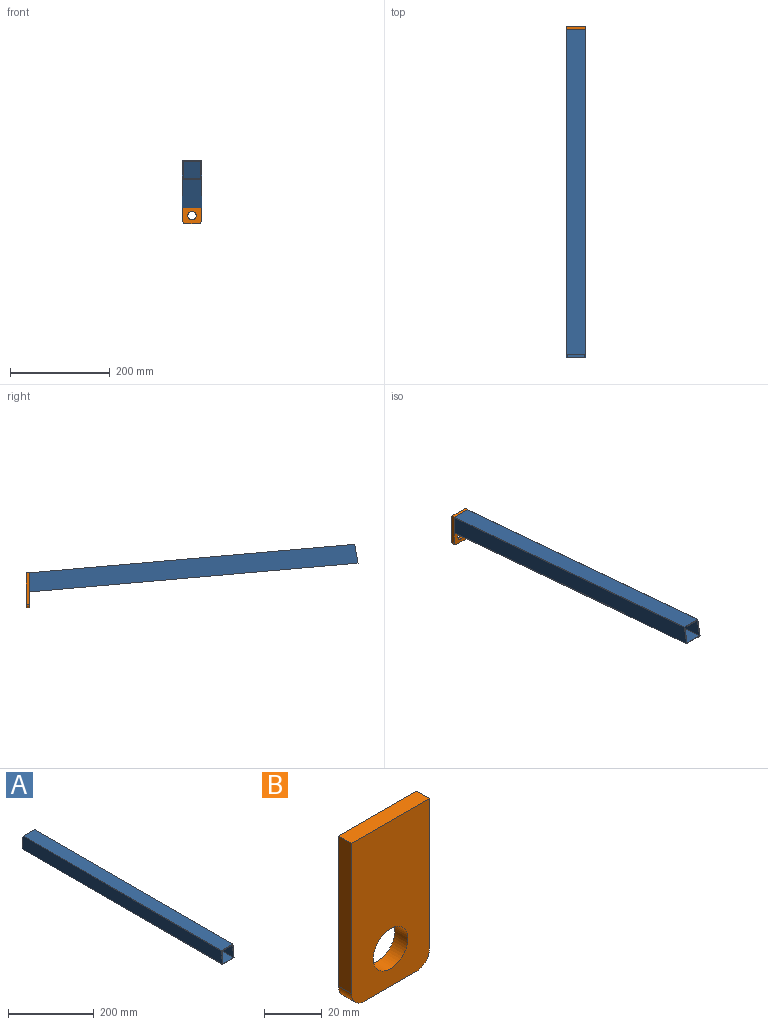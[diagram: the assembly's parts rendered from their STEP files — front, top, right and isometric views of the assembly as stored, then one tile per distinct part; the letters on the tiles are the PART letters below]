
ASSEMBLY  parts=2 mates=1
PART A: 10 faces, bbox 38.1x660.4x38.1 mm
  f0: plane 660.4x38.1mm, normal (1,0,0), area 25034.2mm2, adj f1,f7,f8,f9
  f1: plane 653.73x38.1mm, normal (0,0,1), area 24907.2mm2, adj f0,f5,f8,f9
  f2: plane 660.12x34.93mm, normal (1,0,0), area 22948.1mm2, adj f3,f6,f8,f9
  f3: plane 654.01x34.93mm, normal (0,0,-1), area 22841.3mm2, adj f2,f4,f8,f9
  f4: plane 660.12x34.93mm, normal (-1,0,0), area 22948.1mm2, adj f3,f6,f8,f9
  f5: plane 660.4x38.1mm, normal (-1,0,0), area 25034.2mm2, adj f1,f7,f8,f9
  f6: plane 660.12x34.93mm, normal (0,0,1), area 23054.8mm2, adj f2,f4,f8,f9
  f7: plane 660.4x38.1mm, normal (0,0,-1), area 25161.2mm2, adj f0,f5,f8,f9
  f8: plane 38.1x38.1mm, normal (0,1,0.09), area 232.7mm2, adj f0,f1,f2,f3,f4,f5,f6,f7
  f9: plane 38.1x38.1mm, normal (0,-1,0.09), area 232.7mm2, adj f0,f1,f2,f3,f4,f5,f6,f7
PART B: 9 faces, bbox 38.1x6.4x69.9 mm
  f0: plane 63.5x6.35mm, normal (-1,0,0), area 403.2mm2, adj f1,f5,f6,f7
  f1: cylinder r=6.35mm len=6.35mm, axis (0,1,0), area 63.3mm2, adj f0,f2,f6,f7
  f2: plane 25.4x6.35mm, normal (0,0,-1), area 161.3mm2, adj f1,f3,f6,f7
  f3: cylinder r=6.35mm len=6.35mm, axis (0,1,0), area 63.3mm2, adj f2,f4,f6,f7
  f4: plane 63.5x6.35mm, normal (1,0,0), area 403.2mm2, adj f3,f5,f6,f7
  f5: plane 38.1x6.35mm, normal (0,0,1), area 241.9mm2, adj f0,f4,f6,f7
  f6: plane 69.85x38.1mm, normal (0,-1,0), area 2418.7mm2, adj f0,f1,f2,f3,f4,f5,f8
  f7: plane 69.85x38.1mm, normal (0,1,0), area 2418.7mm2, adj f0,f1,f2,f3,f4,f5,f8
  f8: cylinder r=8.47mm len=16.94mm, axis (0,-1,0), area 337.9mm2, adj f6,f7
PLACE A rot(axis=(-1,0,0),5deg) t=(-107.46,304.41,-39.4)mm
PLACE B t=(-99.9,310.17,-46.64)mm
MATE planar A.f8 <-> B.f6  axis (0,1,0) through (-143.96,303.82,-26.96)mm
